# Revit family: 603-A-4100-DN400
name_source: partatom
category: Pipe Accessories
units: mm (PartAtom-declared; Revit-internal decimal feet)

## family parameters
Always vertical = Yes
Cut with Voids When Loaded = No
Part Type = Valve - Breaks Into
Round Connector Dimension = Use Diameter
Shared = No
Work Plane-Based = No

## types (3) — shared parameters
Bolt_ref = 198 mm  [stored 0.649606 ft]
Bolt_width = 20 mm  [stored 0.0656168 ft]
Bottm_cut = 242 mm  [stored 0.793963 ft]
Bottm_height = 6 mm  [stored 0.019685 ft]
Bottom_Flange_Thicckness = 12 mm  [stored 0.0393701 ft]
D2 = 231 mm
D3 = 254 mm
D4 = 277 mm  [stored 0.908793 ft]
DN400_410- 436 = 603-436-000-4100
DN400_410-436 = 603-436-002-4100
DN400_436-462 = 603-462-000-4100
Description_ = AVK UNIVERSAL SUPA® FLANGE ADAPTOR
H1 = 33 mm  [stored 0.108268 ft]
ID = 160 mm  [stored 0.524934 ft]
L = 220 mm  [stored 0.721785 ft]
L1 = 100 mm  [stored 0.328084 ft]
L3 = 158 mm
Length = 165 mm  [stored 0.541339 ft]
Nomianal_Diameter(DN) = 400 mm  [stored 1.31234 ft]
Nut = 10 mm  [stored 0.0328084 ft]
PCD = 530 mm  [stored 1.73885 ft]
Rib_Thickness = 5 mm  [stored 0.0164042 ft]
Rib_length = 32 mm  [stored 0.104987 ft]
Rib_width = 556 mm  [stored 1.82415 ft]
Search_table = 603-A-4100-DN400
URL product pages = https://www.avkvalves.com
Washer = 3 mm  [stored 0.00984252 ft]
Washer_ref = 188 mm  [stored 0.616798 ft]

## per-type parameters (varying)
| type | D |
| 603-436-000-4100_DN400 | 299 mm |
| 603-436-002-4100_DN400 | 289 mm  [stored 0.948163 ft] |
| 603-462-000-4100_DN400 | 299 mm |

note: [stored X ft] marks values corroborated as IEEE doubles in the binary element streams (Revit-internal decimal feet)

## geometry (parser evidence)
native form markers: Sweep x4
no freeform markers — native parametric forms only
